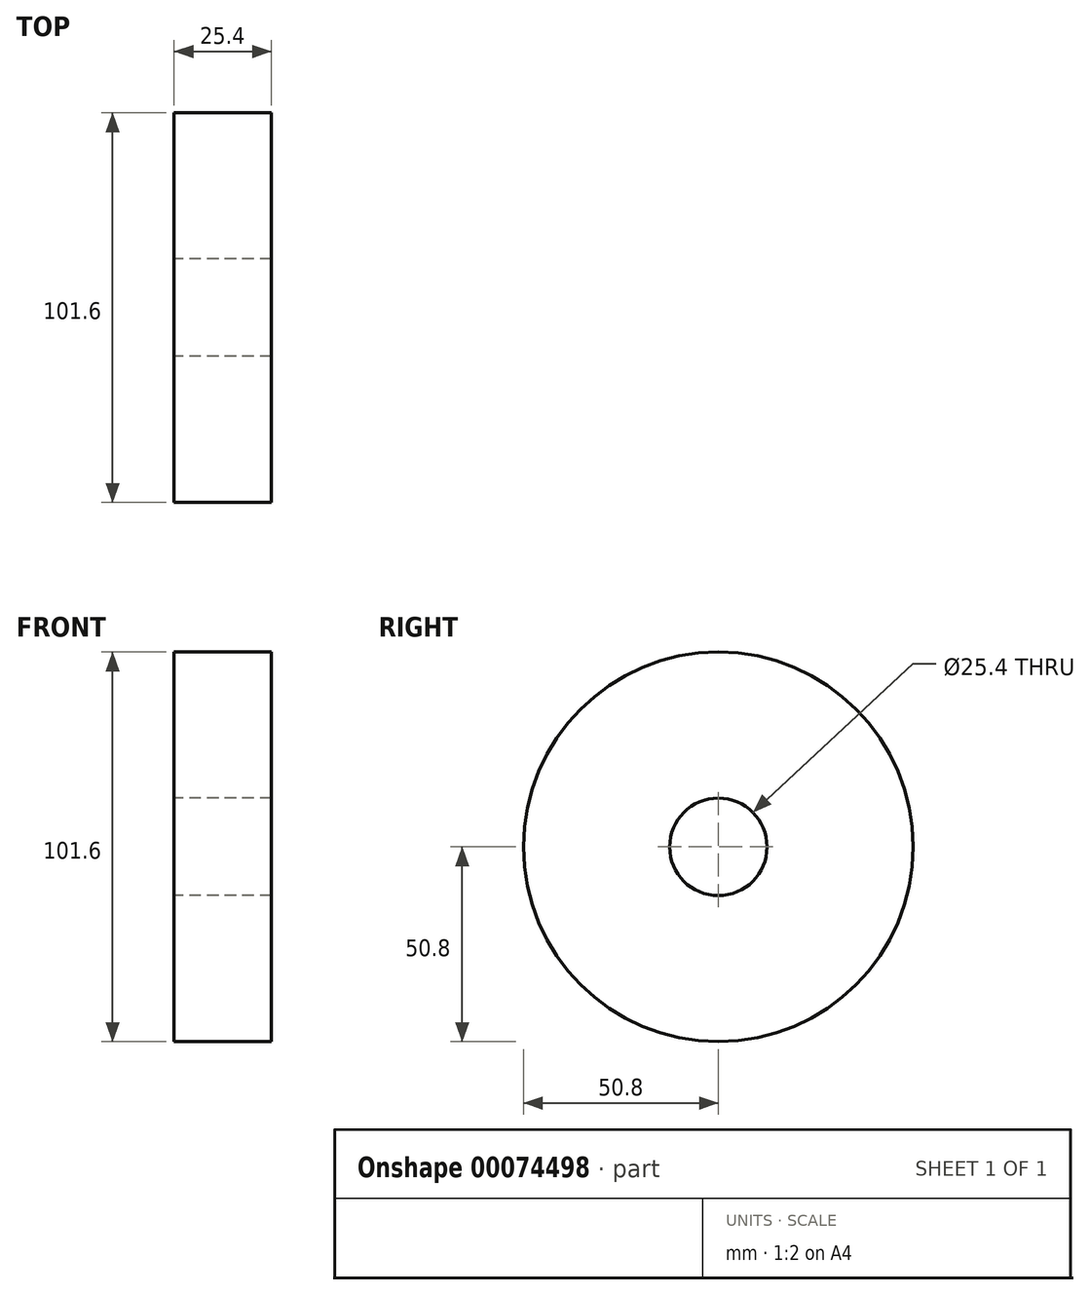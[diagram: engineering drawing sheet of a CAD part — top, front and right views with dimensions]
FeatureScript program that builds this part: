
annotation { "Feature Type Name" : "Feature", "Feature Type Description" : "" }
export const myFeature = defineFeature(function(context is Context, id is Id, definition is map)
    precondition{}
    {
        {
            var Q0;
            Q0=qCreatedBy(makeId("Right.planeOp"),FACE);
            var sketch = newSketch(context, id + "F0", { "sketchPlane" : qUnion([Q0])});
            skCircle(sketch, "E0", {"center": v(0, 0) * mm, "radius": 50.8 * mm});
            skCircle(sketch, "E1", {"center": v(0, 0) * mm, "radius": 12.7 * mm});
            skSolve(sketch);
        }
        {
            var Q0;
            Q0=makeQuery(id+"F0.imprint","IMPRINT",FACE,{"disambiguationData":[TD([[makeQuery(id+"F0.imprint","IMPRINT",EDGE,{"derivedFrom":sQuery(id+"F0.wireOp",EDGE,"E0")}),1.0]])]});
            extrude(context, id + "F1", {"entities" : qUnion([Q0]), "depth" : 25.4 * mm, "offsetDistance" : 25.4 * mm});
        }
    });
